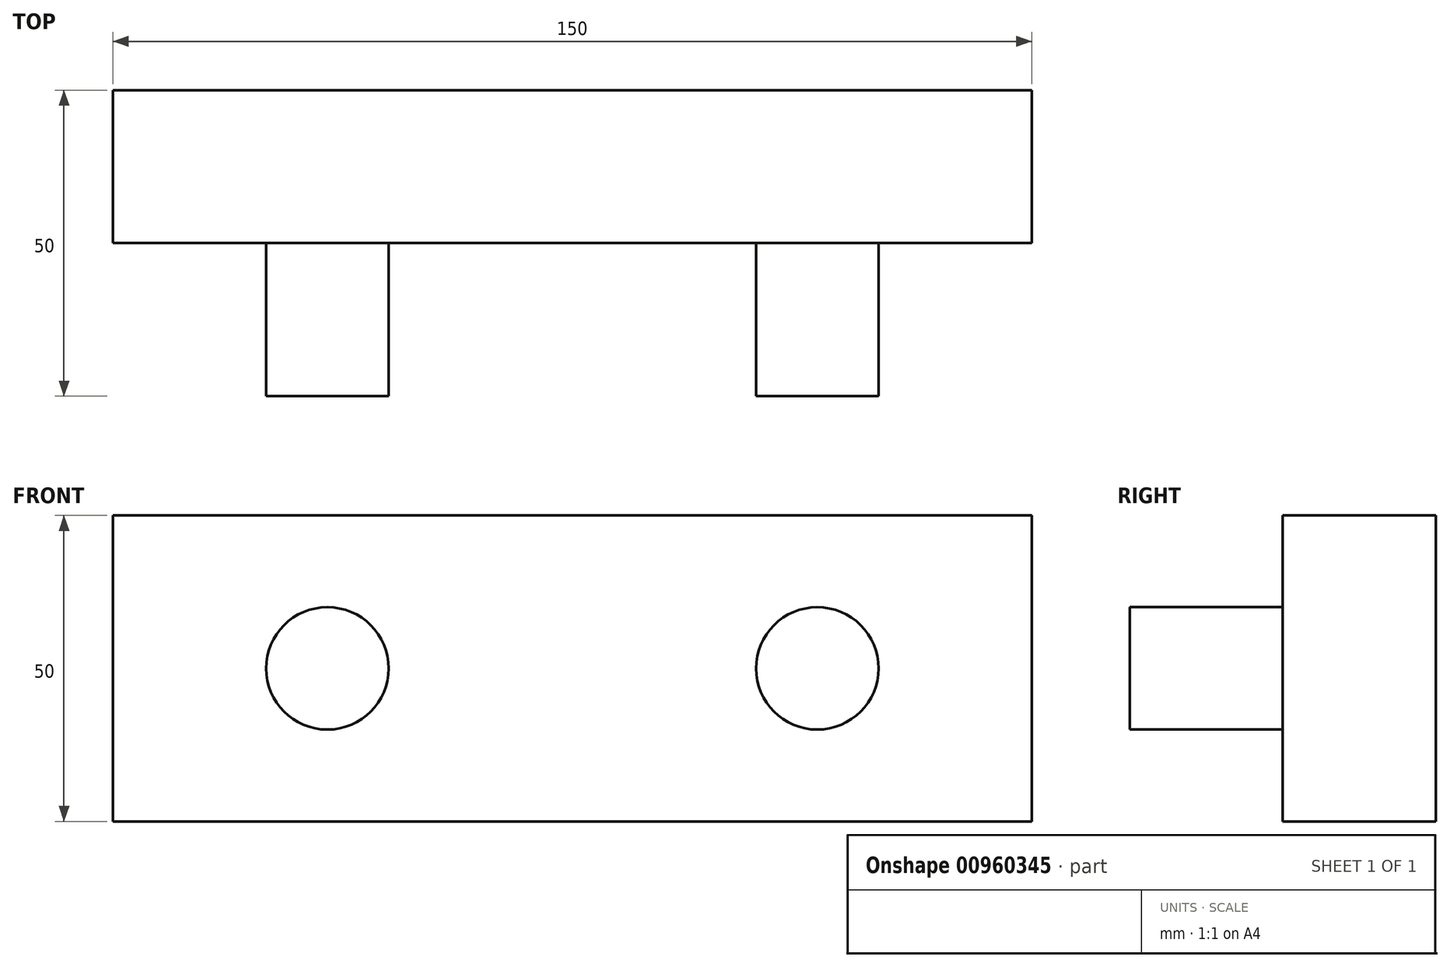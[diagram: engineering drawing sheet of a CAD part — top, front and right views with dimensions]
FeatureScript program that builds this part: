
annotation { "Feature Type Name" : "Feature", "Feature Type Description" : "" }
export const myFeature = defineFeature(function(context is Context, id is Id, definition is map)
    precondition{}
    {
        {
            var Q0;
            Q0=qCreatedBy(makeId("Front.planeOp"),FACE);
            var sketch = newSketch(context, id + "F0", { "sketchPlane" : qUnion([Q0])});
            skLineSegment(sketch, "E0.bottom", {"start": v(-75, 25) * mm, "end": v(75, 25) * mm});
            skLineSegment(sketch, "E0.top", {"start": v(-75, -25) * mm, "end": v(75, -25) * mm});
            skLineSegment(sketch, "E0.left", {"start": v(-75, 25) * mm, "end": v(-75, -25) * mm});
            skLineSegment(sketch, "E0.right", {"start": v(75, 25) * mm, "end": v(75, -25) * mm});
            skCircle(sketch, "E1", {"center": v(-40, 0) * mm, "radius": 10 * mm});
            skCircle(sketch, "E2", {"center": v(40, 0) * mm, "radius": 10 * mm});
            skLineSegment(sketch, "E3", {"start": v(0, 25) * mm, "end": v(0, -25) * mm, "construction": true});
            skLineSegment(sketch, "E4", {"start": v(-75, 0) * mm, "end": v(75, 0) * mm, "construction": true});
            skPoint(sketch, "E5", {"position": v(0, -25) * mm});
            skSolve(sketch);
        }
        {
            var Q0;
            Q0=makeQuery(id+"F0.imprint","IMPRINT",FACE,{"disambiguationData":[TD([[makeQuery(id+"F0.imprint","IMPRINT",EDGE,{"derivedFrom":sQuery(id+"F0.wireOp",EDGE,"E0.bottom")}),-1.0]])]});
            var Q1;
            Q1=makeQuery(id+"F0.imprint","IMPRINT",FACE,{"disambiguationData":[TD([[makeQuery(id+"F0.imprint","IMPRINT",EDGE,{"derivedFrom":sQuery(id+"F0.wireOp",EDGE,"E1")}),1.0]])]});
            var Q2;
            Q2=makeQuery(id+"F0.imprint","IMPRINT",FACE,{"disambiguationData":[TD([[makeQuery(id+"F0.imprint","IMPRINT",EDGE,{"derivedFrom":sQuery(id+"F0.wireOp",EDGE,"E2")}),1.0]])]});
            extrude(context, id + "F1", {"entities" : qUnion([Q0, Q1, Q2]), "oppositeDirection" : true, "depth" : 25 * mm, "offsetDistance" : 25 * mm});
        }
        {
            var Q0;
            Q0=makeQuery(id+"F0.imprint","IMPRINT",FACE,{"disambiguationData":[TD([[makeQuery(id+"F0.imprint","IMPRINT",EDGE,{"derivedFrom":sQuery(id+"F0.wireOp",EDGE,"E1")}),1.0]])]});
            var Q1;
            Q1=makeQuery(id+"F0.imprint","IMPRINT",FACE,{"disambiguationData":[TD([[makeQuery(id+"F0.imprint","IMPRINT",EDGE,{"derivedFrom":sQuery(id+"F0.wireOp",EDGE,"E2")}),1.0]])]});
            extrude(context, id + "F2", {"entities" : qUnion([Q0, Q1]), "operationType" : NewBodyOperationType.ADD, "depth" : 25 * mm, "offsetDistance" : 25 * mm});
        }
    });
